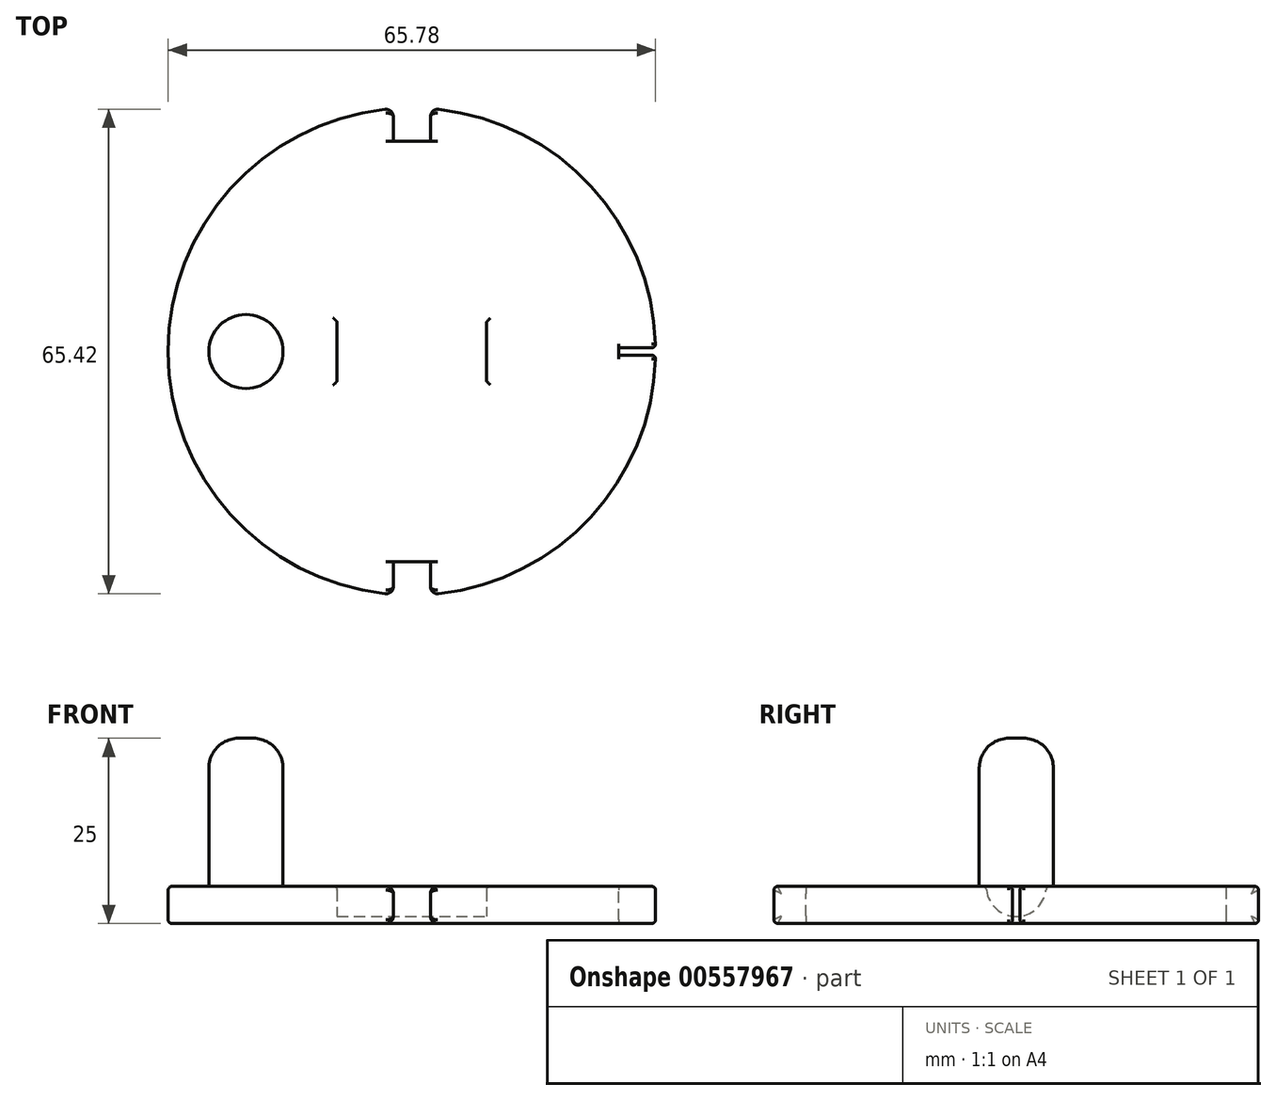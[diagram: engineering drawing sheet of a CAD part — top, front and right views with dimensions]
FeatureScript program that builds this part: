
annotation { "Feature Type Name" : "Feature", "Feature Type Description" : "" }
export const myFeature = defineFeature(function(context is Context, id is Id, definition is map)
    precondition{}
    {
        {
            var Q0;
            Q0=qCreatedBy(makeId("Top.planeOp"),FACE);
            var sketch = newSketch(context, id + "F0", { "sketchPlane" : qUnion([Q0])});
            skCircle(sketch, "E0", {"center": v(0, 0) * mm, "radius": 32.9 * mm});
            skSolve(sketch);
        }
        {
            var Q0;
            Q0=qSketchRegion(id+"F0",true);
            extrude(context, id + "F1", {"entities" : qUnion([Q0]), "depth" : 5 * mm, "offsetDistance" : 25 * mm});
        }
        {
            var Q0;
            Q0=makeQuery(id+"F1.opExtrude","CAP_FACE",FACE,{"disambiguationData":[OSD([sQuery(id+"F0.wireOp",EDGE,"E0")])],"isStart":false});
            var Q1;
            Q1=makeQuery(id+"F1.opExtrude","CAP_FACE",FACE,{"disambiguationData":[OSD([sQuery(id+"F0.wireOp",EDGE,"E0")])],"isStart":true});
            fillet(context, id + "F2", {"entities" : qUnion([Q0, Q1]), "radius" : 0.5 * mm, "tangentPropagation" : true, "allowEdgeOverflow" : false});
        }
        {
            var Q0;
            Q0=makeQuery(id+"F1.opExtrude","CAP_FACE",FACE,{"disambiguationData":[OSD([sQuery(id+"F0.wireOp",EDGE,"E0")])],"isStart":false});
            var sketch = newSketch(context, id + "F3", { "sketchPlane" : qUnion([Q0])});
            skLineSegment(sketch, "E1.bottom", {"start": v(-2.5, 33.4) * mm, "end": v(2.5, 33.4) * mm});
            skLineSegment(sketch, "E1.top", {"start": v(-2.5, 28.4) * mm, "end": v(2.5, 28.4) * mm});
            skLineSegment(sketch, "E1.left", {"start": v(-2.5, 33.4) * mm, "end": v(-2.5, 28.4) * mm});
            skLineSegment(sketch, "E1.right", {"start": v(2.5, 33.4) * mm, "end": v(2.5, 28.4) * mm});
            skPoint(sketch, "E1.middle", {"position": v(0, 30.9) * mm});
            skLineSegment(sketch, "E2.MirrorCS", {"start": v(-2.5, -28.4) * mm, "end": v(2.5, -28.4) * mm});
            skLineSegment(sketch, "E3.MirrorCS", {"start": v(-2.5, -33.4) * mm, "end": v(2.5, -33.4) * mm});
            skLineSegment(sketch, "E4.MirrorCS", {"start": v(-2.5, -33.4) * mm, "end": v(-2.5, -28.4) * mm});
            skPoint(sketch, "E5.MirrorP", {"position": v(0, -30.9) * mm});
            skLineSegment(sketch, "E6.MirrorCS", {"start": v(2.5, -33.4) * mm, "end": v(2.5, -28.4) * mm});
            skSolve(sketch);
        }
        {
            var Q0;
            Q0=qSketchRegion(id+"F3",true);
            extrude(context, id + "F4", {"entities" : qUnion([Q0]), "operationType" : NewBodyOperationType.REMOVE, "endBound" : BoundingType.THROUGH_ALL, "oppositeDirection" : true, "depth" : 25 * mm, "offsetDistance" : 25 * mm});
        }
        {
            var Q0;
            Q0=makeQuery(id+"F4.boolean.opBoolean","INTERSECT",EDGE,{"derivedFrom":[makeQuery(id+"F1.opExtrude","SWEPT_FACE",FACE,{"disambiguationData":[OSD([sQuery(id+"F0.wireOp",EDGE,"E0")])]}),makeQuery(id+"F4.opExtrude","SWEPT_FACE",FACE,{"disambiguationData":[OSD([sQuery(id+"F3.wireOp",EDGE,"E4.MirrorCS")])]})]});
            var Q1;
            Q1=makeQuery(id+"F4.boolean.opBoolean","INTERSECT",EDGE,{"derivedFrom":[makeQuery(id+"F1.opExtrude","SWEPT_FACE",FACE,{"disambiguationData":[OSD([sQuery(id+"F0.wireOp",EDGE,"E0")])]}),makeQuery(id+"F4.opExtrude","SWEPT_FACE",FACE,{"disambiguationData":[OSD([sQuery(id+"F3.wireOp",EDGE,"E6.MirrorCS")])]})]});
            var Q2;
            Q2=makeQuery(id+"F4.boolean.opBoolean","INTERSECT",EDGE,{"derivedFrom":[makeQuery(id+"F1.opExtrude","SWEPT_FACE",FACE,{"disambiguationData":[OSD([sQuery(id+"F0.wireOp",EDGE,"E0")])]}),makeQuery(id+"F4.opExtrude","SWEPT_FACE",FACE,{"disambiguationData":[OSD([sQuery(id+"F3.wireOp",EDGE,"E1.left")])]})]});
            var Q3;
            Q3=makeQuery(id+"F4.boolean.opBoolean","INTERSECT",EDGE,{"derivedFrom":[makeQuery(id+"F1.opExtrude","SWEPT_FACE",FACE,{"disambiguationData":[OSD([sQuery(id+"F0.wireOp",EDGE,"E0")])]}),makeQuery(id+"F4.opExtrude","SWEPT_FACE",FACE,{"disambiguationData":[OSD([sQuery(id+"F3.wireOp",EDGE,"E1.right")])]})]});
            fillet(context, id + "F5", {"entities" : qUnion([Q0, Q1, Q2, Q3]), "radius" : 1 * mm, "tangentPropagation" : true, "allowEdgeOverflow" : false});
        }
        {
            var Q0;
            Q0=makeQuery(id+"F1.opExtrude","CAP_FACE",FACE,{"disambiguationData":[OSD([sQuery(id+"F0.wireOp",EDGE,"E0")])],"isStart":false});
            var sketch = newSketch(context, id + "F6", { "sketchPlane" : qUnion([Q0])});
            skCircle(sketch, "E7", {"center": v(-22.4, 0) * mm, "radius": 5 * mm});
            skSolve(sketch);
        }
        {
            var Q0;
            Q0=qSketchRegion(id+"F6",true);
            extrude(context, id + "F7", {"entities" : qUnion([Q0]), "operationType" : NewBodyOperationType.ADD, "depth" : 20 * mm, "offsetDistance" : 25 * mm});
        }
        {
            var Q0;
            Q0=makeQuery(id+"F7.opExtrude","CAP_FACE",FACE,{"disambiguationData":[OSD([sQuery(id+"F6.wireOp",EDGE,"E7")])],"isStart":false});
            var Q1;
            Q1=makeQuery(id+"F7.opExtrude","CAP_EDGE",EDGE,{"disambiguationData":[OSD([sQuery(id+"F6.wireOp",EDGE,"E7")])],"isStart":true});
            fillet(context, id + "F8", {"entities" : qUnion([Q0, Q1]), "radius" : 4 * mm, "tangentPropagation" : true, "allowEdgeOverflow" : false});
        }
        {
            var Q0;
            Q0=makeQuery(id+"F1.opExtrude","CAP_FACE",FACE,{"disambiguationData":[OSD([sQuery(id+"F0.wireOp",EDGE,"E0")])],"isStart":false});
            var sketch = newSketch(context, id + "F9", { "sketchPlane" : qUnion([Q0])});
            skLineSegment(sketch, "E8.bottom", {"start": v(32.9, -0.5) * mm, "end": v(27.9, -0.5) * mm});
            skLineSegment(sketch, "E8.top", {"start": v(32.9, 0.5) * mm, "end": v(27.9, 0.5) * mm});
            skLineSegment(sketch, "E8.left", {"start": v(32.9, -0.5) * mm, "end": v(32.9, 0.5) * mm});
            skLineSegment(sketch, "E8.right", {"start": v(27.9, -0.5) * mm, "end": v(27.9, 0.5) * mm});
            skPoint(sketch, "E8.middle", {"position": v(30.4, 0) * mm});
            skPoint(sketch, "E8.middle.positionSnap0", {"position": v(32.4, 0) * mm});
            skPoint(sketch, "E8.centerSnap0", {"position": v(32.4, 0) * mm});
            skSolve(sketch);
        }
        {
            var Q0;
            {var subQ0=sQuery(id+"F9.wireOp",EDGE,"E8.right");Q0=makeQuery(id+"F9.imprint","IMPRINT",FACE,{"disambiguationData":[TD([[makeQuery(id+"F9.imprint","IMPRINT",EDGE,{"derivedFrom":subQ0}),-1.0]])]});}
            var Q1;
            Q1=qSketchRegion(id+"F9",true);
            extrude(context, id + "F10", {"entities" : qUnion([Q0, Q1]), "operationType" : NewBodyOperationType.REMOVE, "endBound" : BoundingType.THROUGH_ALL, "oppositeDirection" : true, "depth" : 25 * mm, "offsetDistance" : 25 * mm});
        }
        {
            var Q0;
            Q0=makeQuery(id+"F10.boolean.opBoolean","INTERSECT",EDGE,{"derivedFrom":[makeQuery(id+"F1.opExtrude","CAP_FACE",FACE,{"disambiguationData":[OSD([sQuery(id+"F0.wireOp",EDGE,"E0")])],"isStart":true}),makeQuery(id+"F10.opExtrude","SWEPT_FACE",FACE,{"disambiguationData":[OSD([sQuery(id+"F9.wireOp",EDGE,"E8.bottom")])]})]});
            var Q1;
            Q1=makeQuery(id+"F10.boolean.opBoolean","INTERSECT",EDGE,{"derivedFrom":[makeQuery(id+"F1.opExtrude","CAP_FACE",FACE,{"disambiguationData":[OSD([sQuery(id+"F0.wireOp",EDGE,"E0")])],"isStart":true}),makeQuery(id+"F10.opExtrude","SWEPT_FACE",FACE,{"disambiguationData":[OSD([sQuery(id+"F9.wireOp",EDGE,"E8.top")])]})]});
            fillet(context, id + "F11", {"entities" : qUnion([Q0, Q1]), "radius" : 0.5 * mm, "tangentPropagation" : true, "allowEdgeOverflow" : false});
        }
        {
            var Q0;
            Q0=qCreatedBy(makeId("Right.planeOp"),FACE);
            var sketch = newSketch(context, id + "F12", { "sketchPlane" : qUnion([Q0])});
            skCircle(sketch, "E9", {"center": v(0, 5) * mm, "radius": 4.05 * mm});
            skSolve(sketch);
        }
        {
            var Q0;
            Q0=qSketchRegion(id+"F12",true);
            extrude(context, id + "F13", {"entities" : qUnion([Q0]), "operationType" : NewBodyOperationType.REMOVE, "oppositeDirection" : true, "depth" : 10.1 * mm, "offsetDistance" : 25 * mm, "hasSecondDirection" : true, "secondDirectionOppositeDirection" : false, "secondDirectionDepth" : 10.1 * mm});
        }
        {
            var Q0;
            Q0=makeQuery(id+"F13.boolean.opBoolean","INTERSECT",EDGE,{"derivedFrom":[makeQuery(id+"F1.opExtrude","CAP_FACE",FACE,{"disambiguationData":[OSD([sQuery(id+"F0.wireOp",EDGE,"E0")])],"isStart":false}),makeQuery(id+"F13.opExtrude","CAP_FACE",FACE,{"disambiguationData":[OSD([sQuery(id+"F12.wireOp",EDGE,"E9")])],"isStart":true})]});
            var Q1;
            Q1=makeQuery(id+"F13.boolean.opBoolean","INTERSECT",EDGE,{"disambiguationData":[OD(0.0)],"derivedFrom":[makeQuery(id+"F1.opExtrude","CAP_FACE",FACE,{"disambiguationData":[OSD([sQuery(id+"F0.wireOp",EDGE,"E0")])],"isStart":false}),makeQuery(id+"F13.opExtrude","SWEPT_FACE",FACE,{"disambiguationData":[OSD([sQuery(id+"F12.wireOp",EDGE,"E9")])]})]});
            var Q2;
            Q2=makeQuery(id+"F13.boolean.opBoolean","INTERSECT",EDGE,{"disambiguationData":[OD(1.0)],"derivedFrom":[makeQuery(id+"F1.opExtrude","CAP_FACE",FACE,{"disambiguationData":[OSD([sQuery(id+"F0.wireOp",EDGE,"E0")])],"isStart":false}),makeQuery(id+"F13.opExtrude","SWEPT_FACE",FACE,{"disambiguationData":[OSD([sQuery(id+"F12.wireOp",EDGE,"E9")])]})]});
            var Q3;
            Q3=makeQuery(id+"F13.boolean.opBoolean","INTERSECT",EDGE,{"derivedFrom":[makeQuery(id+"F1.opExtrude","CAP_FACE",FACE,{"disambiguationData":[OSD([sQuery(id+"F0.wireOp",EDGE,"E0")])],"isStart":false}),makeQuery(id+"F13.opExtrude","CAP_FACE",FACE,{"disambiguationData":[OSD([sQuery(id+"F12.wireOp",EDGE,"E9")])],"isStart":false})]});
            fillet(context, id + "F14", {"entities" : qUnion([Q0, Q1, Q2, Q3]), "radius" : 0.5 * mm, "tangentPropagation" : true, "allowEdgeOverflow" : false});
        }
    });
